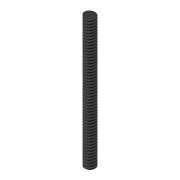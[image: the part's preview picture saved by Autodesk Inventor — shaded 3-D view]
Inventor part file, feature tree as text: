
AUTODESK INVENTOR PART (.ipt)
format: ipt  version: 2020 (Build 240168000, 168)  size: 2,567,168 bytes
history: native  units: mm
features: extrude x1, sketch x1, other x1
ambient origin geometry x8: Origin, YZ Plane, XZ Plane, XY Plane, X Axis, Y Axis, Z Axis, Center Point
bodies: Solid1 (feature_tree)
feature tree (3):
  extrude  "Extrusion1"  [1 undecoded]
  sketch  "Sketch1"  dims[d0=250.0mm d1=0.0mm]
  other  "Cut-Sweep1"
note: 1 required parameter value undecoded (feature->parameter linkage not recoverable at this tier; creation-order binding heuristic only, values carry confidence <= 0.55)
